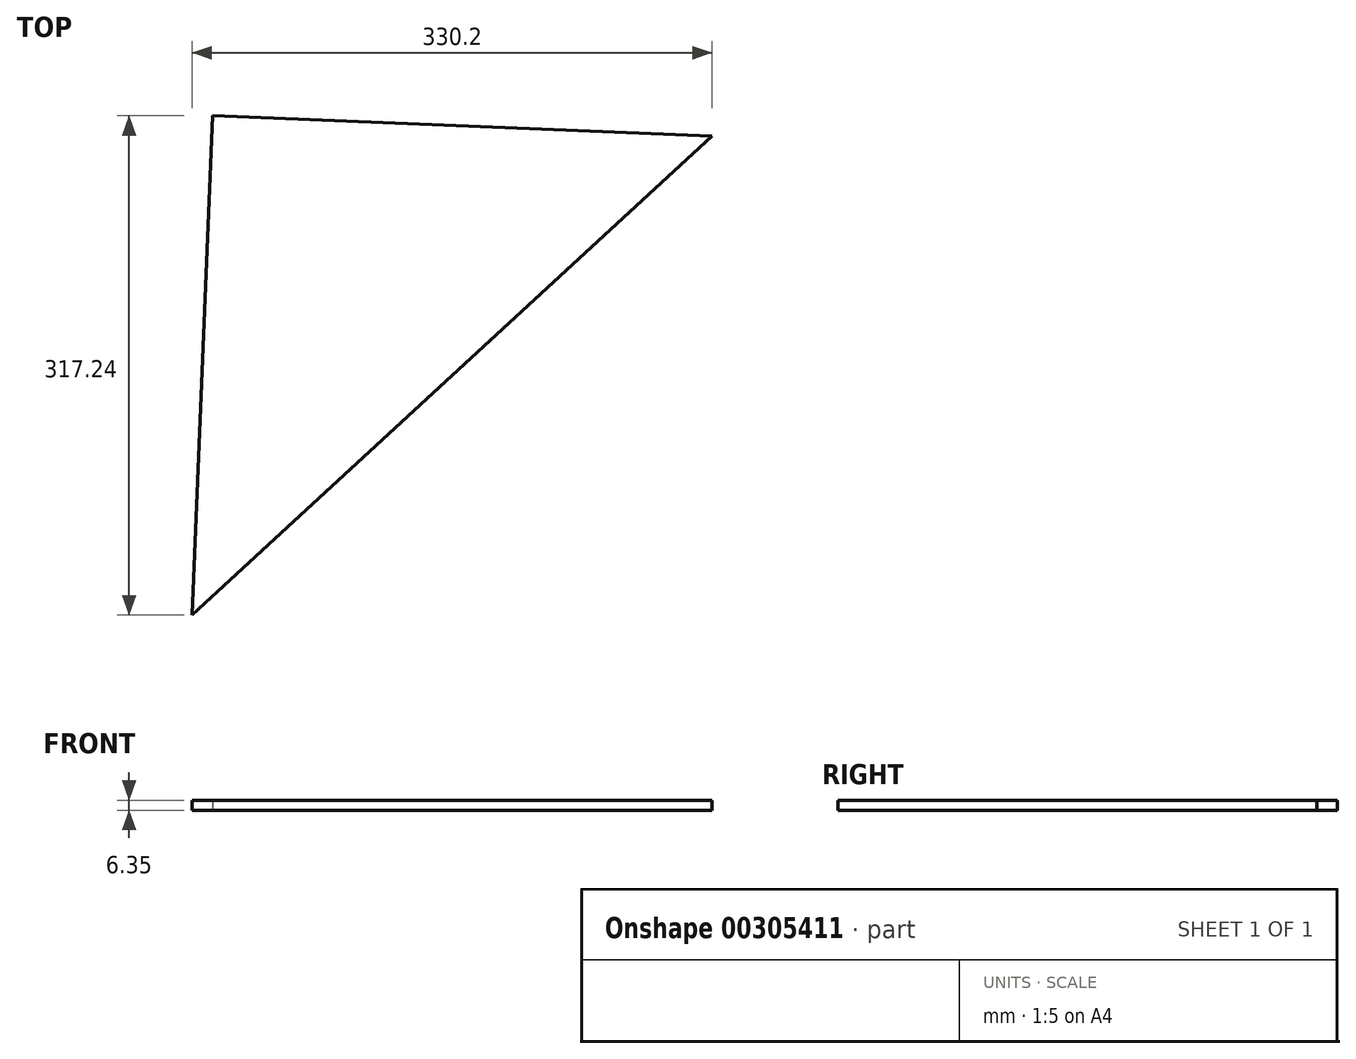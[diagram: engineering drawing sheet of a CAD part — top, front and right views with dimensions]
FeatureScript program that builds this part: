
annotation { "Feature Type Name" : "Feature", "Feature Type Description" : "" }
export const myFeature = defineFeature(function(context is Context, id is Id, definition is map)
    precondition{}
    {
        {
            var Q0;
            Q0=qCreatedBy(makeId("Top.planeOp"),FACE);
            var sketch = newSketch(context, id + "F0", { "sketchPlane" : qUnion([Q0])});
            skLineSegment(sketch, "E0.bottom", {"start": v(-143.23, 131.22) * mm, "end": v(174, 118.26) * mm});
            skLineSegment(sketch, "E0.left", {"start": v(-143.23, 131.22) * mm, "end": v(-156.2, -186.02) * mm});
            skLineSegment(sketch, "E1", {"start": v(-156.2, -186.02) * mm, "end": v(174, 118.26) * mm});
            skSolve(sketch);
        }
        {
            var Q0;
            Q0=makeQuery(id+"F0.imprint","IMPRINT",FACE,{"disambiguationData":[TD([[makeQuery(id+"F0.imprint","IMPRINT",EDGE,{"derivedFrom":sQuery(id+"F0.wireOp",EDGE,"E0.bottom")}),-1.0]])]});
            extrude(context, id + "F1", {"entities" : qUnion([Q0]), "depth" : 6.35 * mm});
        }
    });
